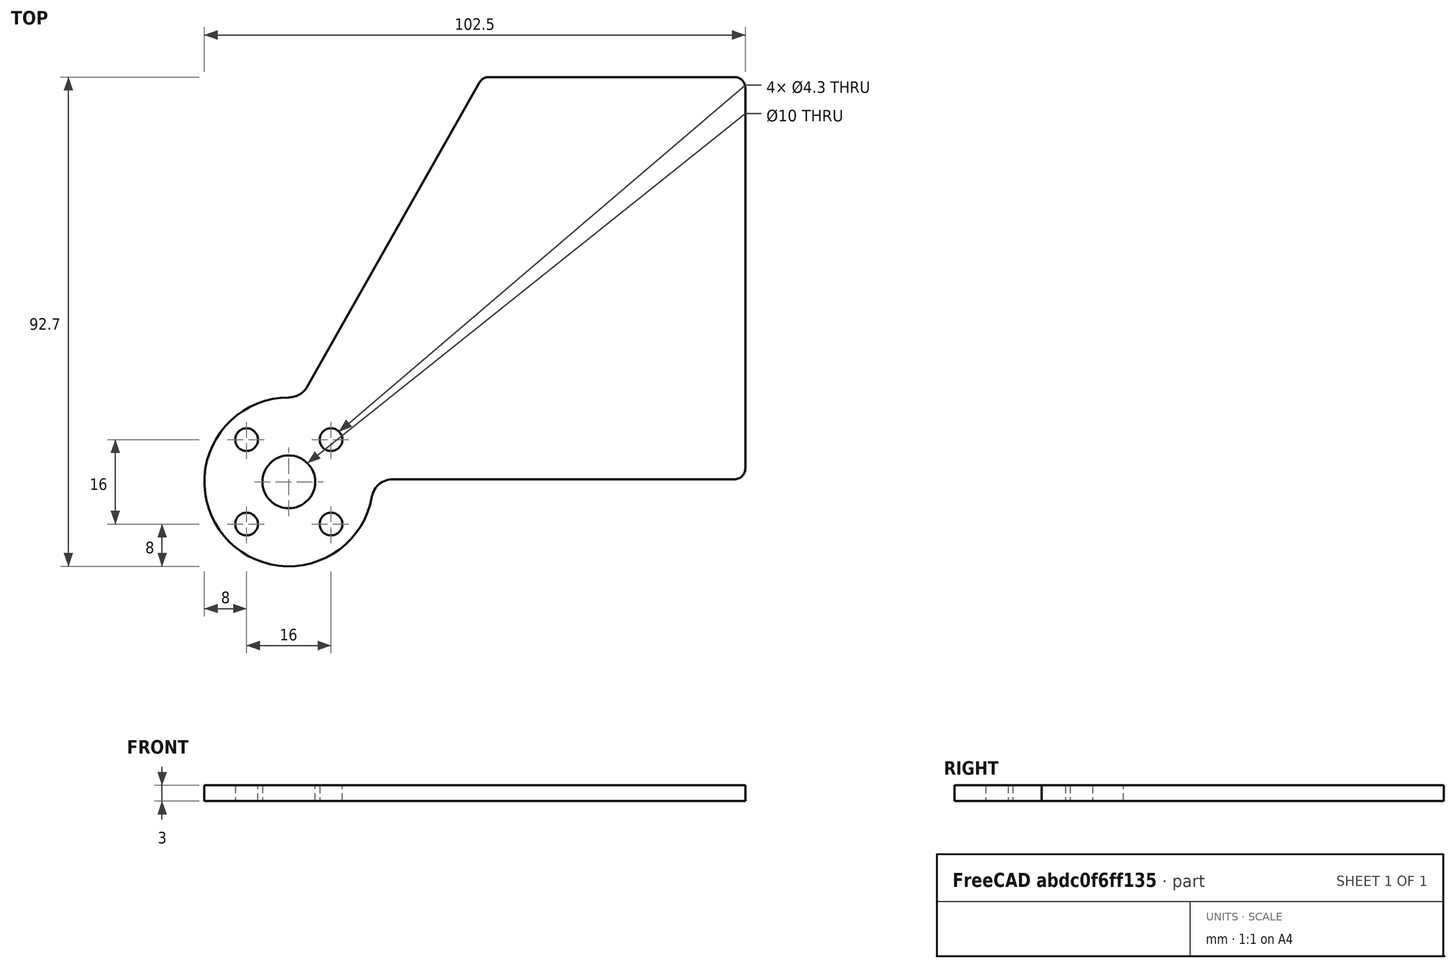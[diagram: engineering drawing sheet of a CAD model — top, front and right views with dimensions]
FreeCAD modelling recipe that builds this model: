
FCSTD DOCUMENT  (FreeCAD 0.21R33675 (Git))
Label: tmaze_door_3in
License: All rights reserved
LicenseURL: http://en.wikipedia.org/wiki/All_rights_reserved
objects: Sketcher::SketchObject×1, Spreadsheet::Sheet×1, PartDesign::Pad×1, PartDesign::Body×1
note: 4 computed .brp shape members not serialized (recipe doc carries the construction recipe); baked Part::Feature solids carry a one-line shape summary decoded from their .brp

FEATURE [Sketcher::SketchObject] Sketch  label="DoorSketch"
  FullyConstrained = true
  MapMode = 5
  Support = -> [XY_Plane]
  expr: Constraints[11] = Spreadsheet.DoorFilletRadius
  expr: Constraints[1] = Spreadsheet.DoorHubDiameter
  expr: Constraints[29] = Spreadsheet.DoorToMazeFloorMargin
  expr: Constraints[34] = Spreadsheet.DoorHubFilletRadius
  expr: Constraints[3] = Spreadsheet.DoorLength
  expr: Constraints[40] = Spreadsheet.ServoSplineToMazeFloorDistance
  expr: Constraints[58] = Spreadsheet.ServoHubMountThruHoleDiameter
  expr: Constraints[59] = Spreadsheet.ServoHubMountHoleSpacing
  expr: Constraints[5] = Spreadsheet.DoorHeight
  expr: Constraints[61] = Spreadsheet.ServoHubCenterHoleDiameter
  sketch-geometry (26):
    g0: Circle CenterX=0 CenterY=0 CenterZ=0 NormalX=0 NormalY=0 NormalZ=1 AngleXU=0 Radius=16
    g1: LineSegment StartX=36.7 StartY=0.5 StartZ=0 EndX=84.5 EndY=0.5 EndZ=0
    g2: LineSegment StartX=86.5 StartY=2.5 StartZ=0 EndX=86.5 EndY=74.7 EndZ=0
    g3: LineSegment StartX=84.5 StartY=76.7 StartZ=0 EndX=37.8659 EndY=76.7 EndZ=0
    g4: LineSegment StartX=3.48079 StartY=18.0292 StartZ=0 EndX=36.1255 EndY=75.6854 EndZ=0
    g5: ArcOfCircle CenterX=84.5 CenterY=2.5 CenterZ=0 NormalX=0 NormalY=0 NormalZ=1 AngleXU=0 Radius=2 StartAngle=4.71239 EndAngle=6.28319
    g6: GeomPoint X=86.5 Y=0.5 Z=0
    g7: ArcOfCircle CenterX=84.5 CenterY=74.7 CenterZ=0 NormalX=0 NormalY=0 NormalZ=1 AngleXU=0 Radius=2 StartAngle=-3.6e-15 EndAngle=1.5708
    g8: GeomPoint X=86.5 Y=76.7 Z=0
    g9: LineSegment StartX=36.7 StartY=76.7 StartZ=0 EndX=36.7 EndY=0.5 EndZ=0
    g10: ArcOfCircle CenterX=37.8659 CenterY=74.7 CenterZ=0 NormalX=0 NormalY=0 NormalZ=1 AngleXU=0 Radius=2 StartAngle=1.5708 EndAngle=2.6264
    g11: GeomPoint X=36.7 Y=76.7 Z=0
    g12: ArcOfCircle CenterX=0 CenterY=0 CenterZ=0 NormalX=0 NormalY=0 NormalZ=1 AngleXU=0 Radius=16 StartAngle=1.5708 EndAngle=6.10728
    g13: LineSegment StartX=36.7 StartY=0 StartZ=0 EndX=36.7 EndY=0.5 EndZ=0
    g14: LineSegment StartX=36.7 StartY=0.5 StartZ=0 EndX=19.6914 EndY=0.5 EndZ=0
    g15: ArcOfCircle CenterX=19.6914 CenterY=-3.5 CenterZ=0 NormalX=0 NormalY=0 NormalZ=1 AngleXU=0 Radius=4 StartAngle=1.5708 EndAngle=2.96569
    g16: ArcOfCircle CenterX=5e-16 CenterY=20 CenterZ=0 NormalX=0 NormalY=0 NormalZ=1 AngleXU=0 Radius=4 StartAngle=4.71239 EndAngle=5.76799
    g17: LineSegment StartX=-8 StartY=8 StartZ=0 EndX=8 EndY=8 EndZ=0
    g18: LineSegment StartX=8 StartY=8 StartZ=0 EndX=8 EndY=-8 EndZ=0
    g19: LineSegment StartX=8 StartY=-8 StartZ=0 EndX=-8 EndY=-8 EndZ=0
    g20: LineSegment StartX=-8 StartY=-8 StartZ=0 EndX=-8 EndY=8 EndZ=0
    g21: Circle CenterX=-8 CenterY=8 CenterZ=0 NormalX=0 NormalY=0 NormalZ=1 AngleXU=0 Radius=2.15
    g22: Circle CenterX=8 CenterY=8 CenterZ=0 NormalX=0 NormalY=0 NormalZ=1 AngleXU=0 Radius=2.15
    g23: Circle CenterX=-8 CenterY=-8 CenterZ=0 NormalX=0 NormalY=0 NormalZ=1 AngleXU=0 Radius=2.15
    g24: Circle CenterX=8 CenterY=-8 CenterZ=0 NormalX=0 NormalY=0 NormalZ=1 AngleXU=0 Radius=2.15
    g25: Circle CenterX=0 CenterY=0 CenterZ=0 NormalX=0 NormalY=0 NormalZ=1 AngleXU=0 Radius=5
  constraints (62):
    c: Coincident(g0,g-1)
    c: Diameter(g0) = 32
    c: Horizontal(g1)
    c: DistanceX(g1,g6) = 49.8
    c: Vertical(g2)
    c: DistanceY(g6,g8) = 76.2
    c: Horizontal(g3)
    c: PointOnObject(g6,g1)
    c: PointOnObject(g6,g2)
    c: Tangent(g1,g5) = -1.5708
    c: Tangent(g2,g5) = -1.5708
    c: Radius(g5) = 2
    c: PointOnObject(g8,g3)
    c: PointOnObject(g8,g2)
    c: Tangent(g3,g7) = -1.5708
    c: Tangent(g2,g7) = -1.5708
    c: Equal(g5,g7)
    c: Coincident(g9,g11)
    c: Vertical(g9)
    c: PointOnObject(g11,g4)
    c: PointOnObject(g11,g3)
    c: Tangent(g4,g10) = 1.5708
    c: Tangent(g3,g10) = -1.5708
    c: Equal(g7,g10)
    c: Coincident(g12,g0)
    c: PointOnObject(g12,g0)
    c: PointOnObject(g13,g-1)
    c: Vertical(g13)
    c: Coincident(g13,g1)
    c: DistanceY(g13,g13) = 0.5
    c: Coincident(g14,g1)
    c: Horizontal(g14)
    c: Tangent(g15,g14) = -1.5708
    c: Tangent(g15,g12) = 1.5708
    c: Radius(g15) = 4
    c: Tangent(g12,g16) = 1.5708
    c: Tangent(g4,g16) = -1.5708
    c: Equal(g16,g15)
    c: PointOnObject(g12,g-2)
    c: Coincident(g9,g1)
    c: DistanceX(g12,g1) = 36.7
    c: Coincident(g17,g18)
    c: Coincident(g18,g19)
    c: Coincident(g19,g20)
    c: Coincident(g20,g17)
    c: Horizontal(g17)
    c: Horizontal(g19)
    c: Vertical(g18)
    c: Vertical(g20)
    c: Symmetric(g17,g18,g12)
    c: Equal(g20,g17)
    c: Coincident(g21,g17)
    c: Coincident(g22,g17)
    c: Coincident(g23,g19)
    c: Coincident(g24,g18)
    c: Equal(g21,g22)
    c: Equal(g22,g24)
    c: Equal(g24,g23)
    c: Diameter(g21) = 4.3
    c: DistanceX(g17,g17) = 16
    c: Coincident(g25,g12)
    c: Diameter(g25) = 10
FEATURE [Spreadsheet::Sheet] Spreadsheet
  cells = A2='Servo Hub Parameters; A3='ServoHubDiameter; B3(ServoHubDiameter)==32 mm; A4='ServoHubMountHoleSpacing; B4(ServoHubMountHoleSpacing)==16 mm; A5='ServoHubMountThruHoleDiameter; B5(ServoHubMountThruHoleDiameter)==4.3 mm; A6='ServoHubCenterHoleDiameter; B6(ServoHubCenterHoleDiameter)==10 mm; A7='ServoSplineToServoMountHoleDistance; B7(ServoSplineToServoMountHoleDistance)==14.2 mm; A8='ServoMountHoleToBracketBndryDistance; B8(ServoMountHoleToBracketBndryDistance)==3.5 mm; A9='ServoMarginToMountPlate; B9(ServoMarginToMountPlate)==10 mm; A10='MountPlateThickness; B10(MountPlateThickness)==9 mm; A11='MazeWidth; B11(MazeWidth)==2 in; A14='Design Parameters; A15='DoorHubDiameter; B15(DoorHubDiameter)==ServoHubDiameter; A16='DoorToMazeFloorMargin; B16(DoorToMazeFloorMargin)==0.5 mm; A17='DoorToMazeWallMargin; B17(DoorToMazeWallMargin)==1 mm; A18='ServoSplineToMazeFloorDistance; B18(ServoSplineToMazeFloorDistance)==ServoSplineToServoMountHoleDistance + ServoMountHoleToBracketBndryDistance + ServoMarginToMountPlate + MountPlateThickness; A19='DoorLength; B19(DoorLength)==MazeWidth - DoorToMazeWallMargin; A20='DoorHeight; B20(DoorHeight)==3 in; A21='DoorFilletRadius; B21(DoorFilletRadius)==2 mm; A22='DoorHubFilletRadius; B22(DoorHubFilletRadius)==4 mm; A23='DoorThickness; B23(DoorThickness)==3 mm
FEATURE [PartDesign::Pad] Pad
  Direction = (0,0,1)
  Length = 3
  Length2 = 10
  Profile = -> Sketch
  ReferenceAxis = -> Sketch [N_Axis]
  Type = 0
  expr: Length = Spreadsheet.DoorThickness
FEATURE [PartDesign::Body] Body
  Group = -> [Sketch,Pad]
  Origin = -> Origin
  Tip = -> Pad
